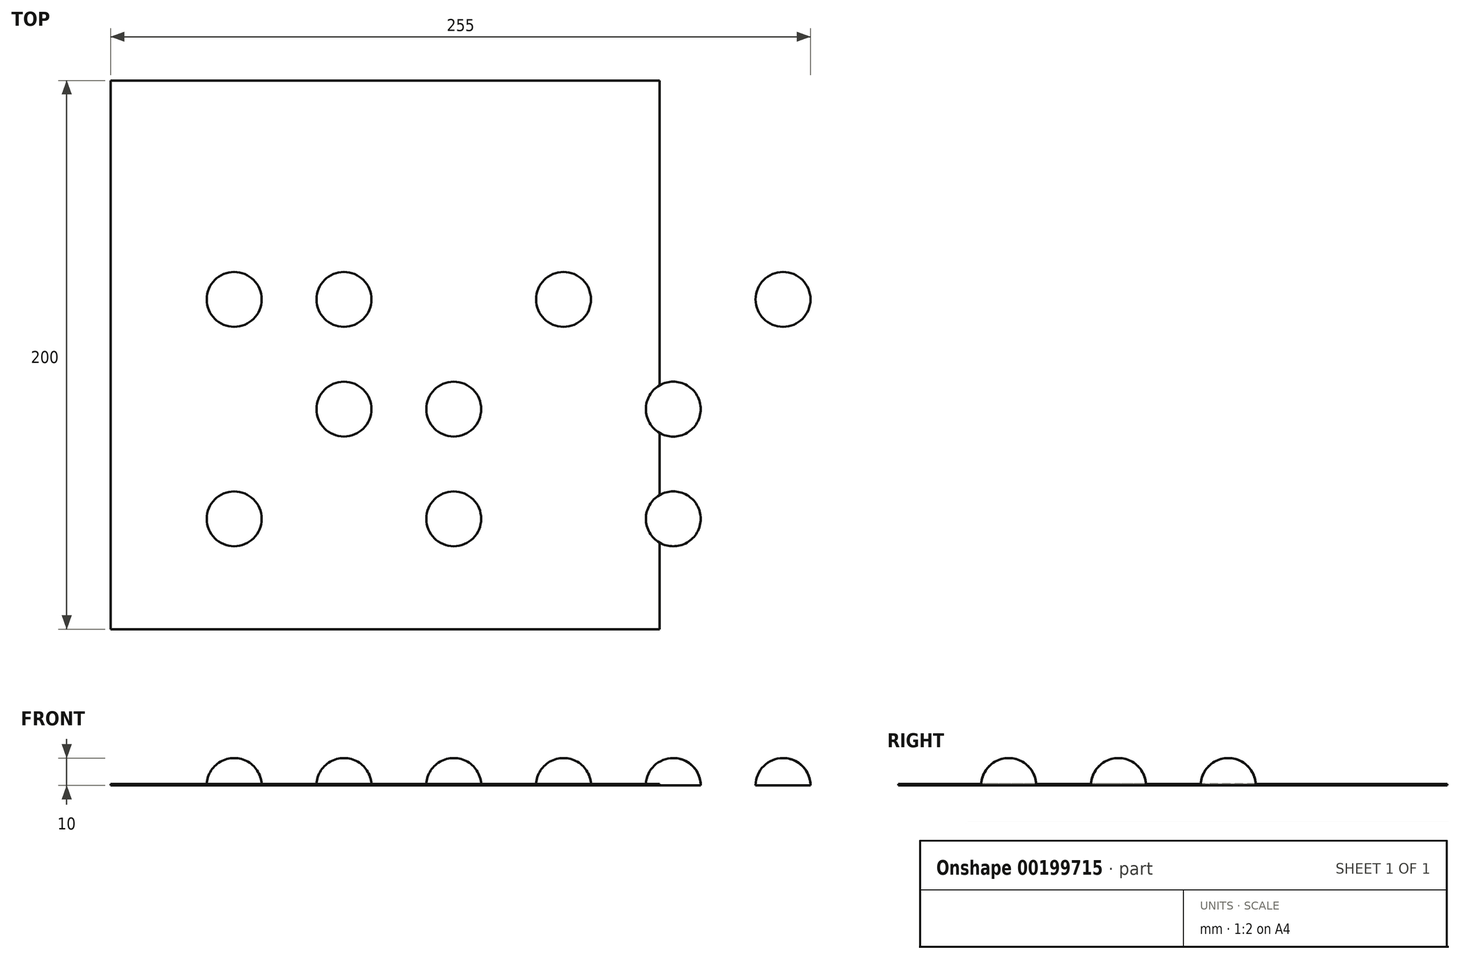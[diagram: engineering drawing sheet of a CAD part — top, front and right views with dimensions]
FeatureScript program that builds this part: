
annotation { "Feature Type Name" : "Feature", "Feature Type Description" : "" }
export const myFeature = defineFeature(function(context is Context, id is Id, definition is map)
    precondition{}
    {
        {
            var Q0;
            Q0=qCreatedBy(makeId("Top.planeOp"),FACE);
            var sketch = newSketch(context, id + "F0", { "sketchPlane" : qUnion([Q0])});
            skLineSegment(sketch, "E0.bottom", {"start": v(-100, 100) * mm, "end": v(100, 100) * mm});
            skLineSegment(sketch, "E0.top", {"start": v(-100, -100) * mm, "end": v(100, -100) * mm});
            skLineSegment(sketch, "E0.left", {"start": v(-100, 100) * mm, "end": v(-100, -100) * mm});
            skLineSegment(sketch, "E0.right", {"start": v(100, 100) * mm, "end": v(100, -100) * mm});
            skPoint(sketch, "E0.middle", {"position": v(0, 0) * mm});
            skSolve(sketch);
        }
        {
            var Q0;
            Q0=makeQuery(id+"F0.imprint","IMPRINT",FACE,{"disambiguationData":[TD([[makeQuery(id+"F0.imprint","IMPRINT",EDGE,{"derivedFrom":sQuery(id+"F0.wireOp",EDGE,"E0.bottom")}),-1.0]])]});
            var sketch = newSketch(context, id + "F1", { "sketchPlane" : qUnion([Q0])});
            skSolve(sketch);
        }
        {
            var Q0;
            Q0=makeQuery(id+"F0.imprint","IMPRINT",FACE,{"disambiguationData":[TD([[makeQuery(id+"F0.imprint","IMPRINT",EDGE,{"derivedFrom":sQuery(id+"F0.wireOp",EDGE,"E0.bottom")}),-1.0]])]});
            var sketch = newSketch(context, id + "F2", { "sketchPlane" : qUnion([Q0])});
            skCircle(sketch, "E1", {"center": v(-55, -59.79) * mm, "radius": 10 * mm});
            skCircle(sketch, "E2.0.2.0", {"center": v(-55, 20.21) * mm, "radius": 10 * mm});
            skCircle(sketch, "E2.1.1.0", {"center": v(-15, -19.79) * mm, "radius": 10 * mm});
            skCircle(sketch, "E2.1.2.0", {"center": v(-15, 20.21) * mm, "radius": 10 * mm});
            skCircle(sketch, "E2.2.0.0", {"center": v(25, -59.79) * mm, "radius": 10 * mm});
            skCircle(sketch, "E2.2.1.0", {"center": v(25, -19.79) * mm, "radius": 10 * mm});
            skCircle(sketch, "E2.3.2.0", {"center": v(65, 20.21) * mm, "radius": 10 * mm});
            skCircle(sketch, "E2.4.0.0", {"center": v(105, -59.79) * mm, "radius": 10 * mm});
            skCircle(sketch, "E2.4.1.0", {"center": v(105, -19.79) * mm, "radius": 10 * mm});
            skCircle(sketch, "E2.5.2.0", {"center": v(145, 20.21) * mm, "radius": 10 * mm});
            skLineSegment(sketch, "E2.direction1", {"start": v(-55, -59.79) * mm, "end": v(-15, -59.79) * mm, "construction": true});
            skLineSegment(sketch, "E2.direction2", {"start": v(-55, -59.79) * mm, "end": v(-55, -19.79) * mm, "construction": true});
            skSolve(sketch);
        }
        {
            var Q0;
            Q0 = qSketchRegion(id + "F0", true);
            extrude(context, id + "F3", {"entities" : qUnion([Q0]), "depth" : 0.5 * mm});
        }
        {
            var Q0;
            Q0 = qSketchRegion(id + "F2", true);
            extrude(context, id + "F4", {"entities" : qUnion([Q0]), "operationType" : NewBodyOperationType.ADD, "depth" : 10 * mm});
        }
        {
            var Q0;
            Q0=makeQuery(id+"F4.opExtrude","CAP_EDGE",EDGE,{"disambiguationData":[OSD([sQuery(id+"F2.wireOp",EDGE,"E1")])],"isStart":false});
            var Q1;
            Q1=makeQuery(id+"F4.opExtrude","CAP_EDGE",EDGE,{"disambiguationData":[OSD([sQuery(id+"F2.wireOp",EDGE,"E2.1.1.0")])],"isStart":false});
            var Q2;
            Q2=makeQuery(id+"F4.opExtrude","CAP_EDGE",EDGE,{"disambiguationData":[OSD([sQuery(id+"F2.wireOp",EDGE,"E2.1.2.0")])],"isStart":false});
            var Q3;
            Q3=makeQuery(id+"F4.opExtrude","CAP_EDGE",EDGE,{"disambiguationData":[OSD([sQuery(id+"F2.wireOp",EDGE,"E2.0.2.0")])],"isStart":false});
            var Q4;
            Q4=makeQuery(id+"F4.opExtrude","CAP_EDGE",EDGE,{"disambiguationData":[OSD([sQuery(id+"F2.wireOp",EDGE,"E2.3.2.0")])],"isStart":false});
            var Q5;
            Q5=makeQuery(id+"F4.opExtrude","CAP_EDGE",EDGE,{"disambiguationData":[OSD([sQuery(id+"F2.wireOp",EDGE,"E2.2.1.0")])],"isStart":false});
            var Q6;
            Q6=makeQuery(id+"F4.opExtrude","CAP_EDGE",EDGE,{"disambiguationData":[OSD([sQuery(id+"F2.wireOp",EDGE,"E2.2.0.0")])],"isStart":false});
            var Q7;
            Q7=makeQuery(id+"F4.opExtrude","CAP_EDGE",EDGE,{"disambiguationData":[OSD([sQuery(id+"F2.wireOp",EDGE,"E2.4.1.0")])],"isStart":false});
            var Q8;
            Q8=makeQuery(id+"F4.opExtrude","CAP_EDGE",EDGE,{"disambiguationData":[OSD([sQuery(id+"F2.wireOp",EDGE,"E2.4.0.0")])],"isStart":false});
            var Q9;
            Q9=makeQuery(id+"F4.opExtrude","CAP_EDGE",EDGE,{"disambiguationData":[OSD([sQuery(id+"F2.wireOp",EDGE,"E2.5.2.0")])],"isStart":false});
            fillet(context, id + "F5", {"entities" : qUnion([Q0, Q1, Q2, Q3, Q4, Q5, Q6, Q7, Q8, Q9]), "radius" : 10 * mm, "tangentPropagation" : true, "allowEdgeOverflow" : false});
        }
    });
